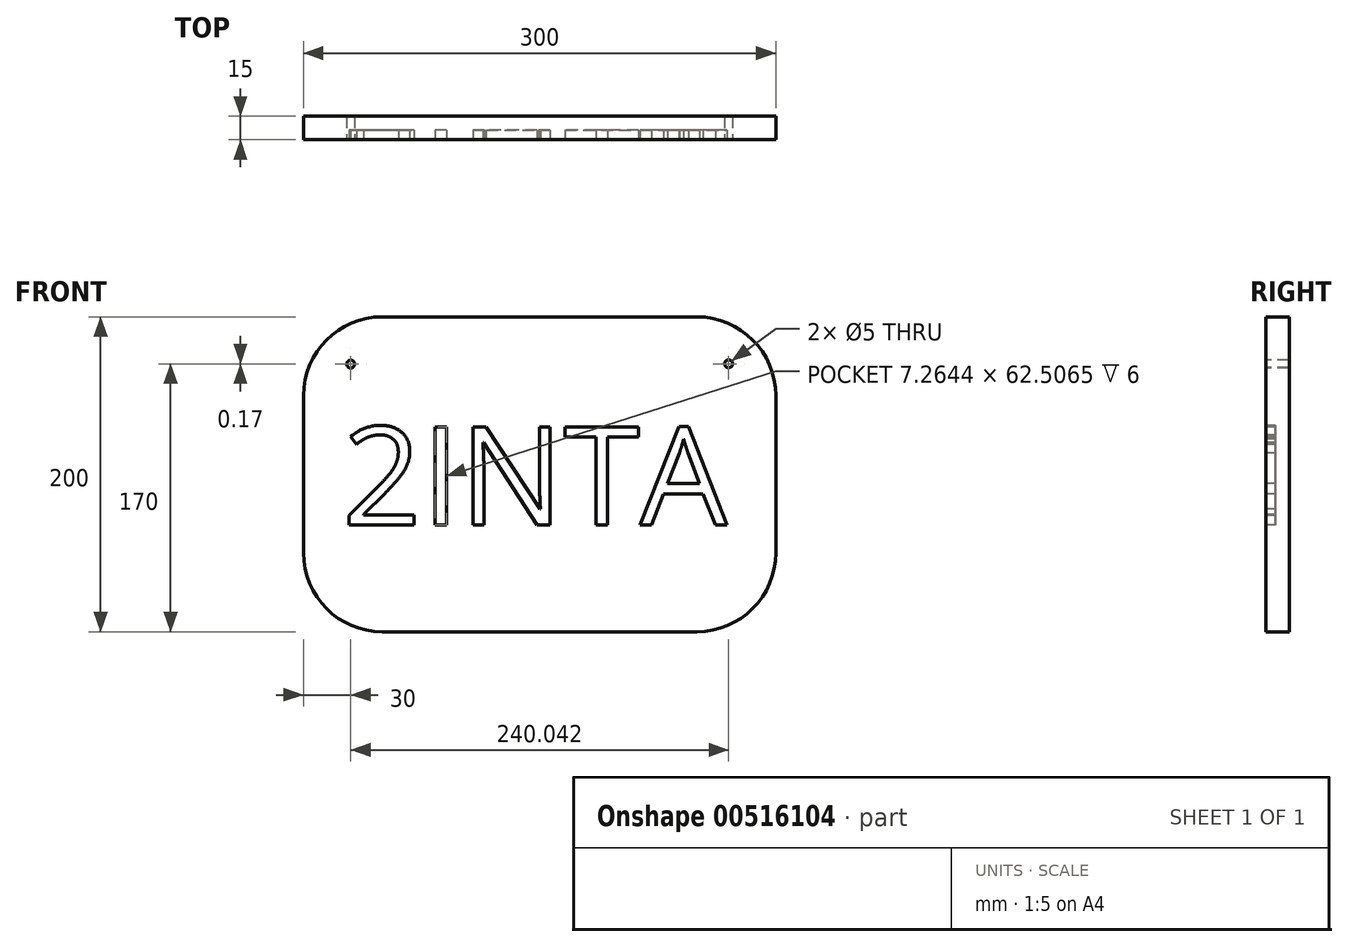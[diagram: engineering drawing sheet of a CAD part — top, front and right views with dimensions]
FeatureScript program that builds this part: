
annotation { "Feature Type Name" : "Feature", "Feature Type Description" : "" }
export const myFeature = defineFeature(function(context is Context, id is Id, definition is map)
    precondition{}
    {
        {
            var Q0;
            Q0=qCreatedBy(makeId("Front.planeOp"),FACE);
            var sketch = newSketch(context, id + "F0", { "sketchPlane" : qUnion([Q0])});
            skLineSegment(sketch, "E0.bottom", {"start": v(150, 100) * mm, "end": v(-150, 100) * mm});
            skLineSegment(sketch, "E0.top", {"start": v(150, -100) * mm, "end": v(-150, -100) * mm});
            skLineSegment(sketch, "E0.left", {"start": v(150, 100) * mm, "end": v(150, -100) * mm});
            skLineSegment(sketch, "E0.right", {"start": v(-150, 100) * mm, "end": v(-150, -100) * mm});
            skPoint(sketch, "E0.middle", {"position": v(0, 0) * mm});
            skSolve(sketch);
        }
        {
            var Q0;
            Q0=makeQuery(id+"F0.imprint","IMPRINT",FACE,{"disambiguationData":[TD([[makeQuery(id+"F0.imprint","IMPRINT",EDGE,{"derivedFrom":sQuery(id+"F0.wireOp",EDGE,"E0.bottom")}),1.0]])]});
            extrude(context, id + "F1", {"entities" : qUnion([Q0]), "depth" : 15 * mm, "offsetDistance" : 25 * mm});
        }
        {
            var Q0;
            Q0=makeQuery(id+"F1.opExtrude","CAP_FACE",FACE,{"disambiguationData":[OSD([sQuery(id+"F0.wireOp",EDGE,"E0.bottom"),sQuery(id+"F0.wireOp",EDGE,"E0.top"),sQuery(id+"F0.wireOp",EDGE,"E0.left"),sQuery(id+"F0.wireOp",EDGE,"E0.right")])],"isStart":false});
            var sketch = newSketch(context, id + "F2", { "sketchPlane" : qUnion([Q0])});
            skText(sketch, "E1", { "text": "2INTA", "fontName": "OpenSans-Regular.ttf"});
            const initialGuessF2  = {"E1": [-0.12516, -0.03234, 1, 0, 0.06304]};
            skSetInitialGuess(sketch, initialGuessF2);
            skSolve(sketch);
        }
        {
            var Q0;
            Q0=makeQuery(id+"F1.opExtrude","SWEPT_EDGE",EDGE,{"disambiguationData":[OSD([sQuery(id+"F0.wireOp",EDGE,"E0.bottom"),sQuery(id+"F0.wireOp",EDGE,"E0.left")])]});
            var Q1;
            Q1=makeQuery(id+"F1.opExtrude","SWEPT_EDGE",EDGE,{"disambiguationData":[OSD([sQuery(id+"F0.wireOp",EDGE,"E0.top"),sQuery(id+"F0.wireOp",EDGE,"E0.left")])]});
            var Q2;
            Q2=makeQuery(id+"F1.opExtrude","SWEPT_EDGE",EDGE,{"disambiguationData":[OSD([sQuery(id+"F0.wireOp",EDGE,"E0.top"),sQuery(id+"F0.wireOp",EDGE,"E0.right")])]});
            var Q3;
            Q3=makeQuery(id+"F1.opExtrude","SWEPT_EDGE",EDGE,{"disambiguationData":[OSD([sQuery(id+"F0.wireOp",EDGE,"E0.bottom"),sQuery(id+"F0.wireOp",EDGE,"E0.right")])]});
            fillet(context, id + "F3", {"entities" : qUnion([Q0, Q1, Q2, Q3]), "radius" : 50 * mm, "tangentPropagation" : true, "allowEdgeOverflow" : false});
        }
        {
            var Q0;
            Q0 = qSketchRegion(id + "F2", true);
            extrude(context, id + "F4", {"entities" : qUnion([Q0]), "operationType" : NewBodyOperationType.REMOVE, "oppositeDirection" : true, "depth" : 6 * mm, "offsetDistance" : 25 * mm});
        }
        {
            var Q0;
            {var subQ0=sQuery(id+"F0.wireOp",EDGE,"E0.right");var subQ1=sQuery(id+"F0.wireOp",EDGE,"E0.bottom");var subQ2=sQuery(id+"F0.wireOp",EDGE,"E0.left");var subQ3=sQuery(id+"F0.wireOp",EDGE,"E0.top");Q0=makeQuery(id+"F4.boolean.opBoolean","SPLIT",FACE,{"disambiguationData":[TD([makeQuery(id+"F1.opExtrude","SWEPT_FACE",FACE,{"disambiguationData":[OSD([subQ1])]})])],"derivedFrom":makeQuery(id+"F1.opExtrude","CAP_FACE",FACE,{"disambiguationData":[OSD([subQ1,subQ3,subQ2,subQ0])],"isStart":false})});}
            var sketch = newSketch(context, id + "F5", { "sketchPlane" : qUnion([Q0])});
            skCircle(sketch, "E2", {"center": v(-120, 70) * mm, "radius": 2.5 * mm});
            skLineSegment(sketch, "E3", {"start": v(0, 100) * mm, "end": v(0.14, -100) * mm, "construction": true});
            skCircle(sketch, "E4.MirrorC", {"center": v(120.04, 70.17) * mm, "radius": 2.5 * mm});
            skSolve(sketch);
        }
        {
            var Q0;
            Q0 = qSketchRegion(id + "F5", true);
            extrude(context, id + "F6", {"entities" : qUnion([Q0]), "operationType" : NewBodyOperationType.REMOVE, "oppositeDirection" : true, "depth" : 25 * mm, "offsetDistance" : 25 * mm});
        }
    });
